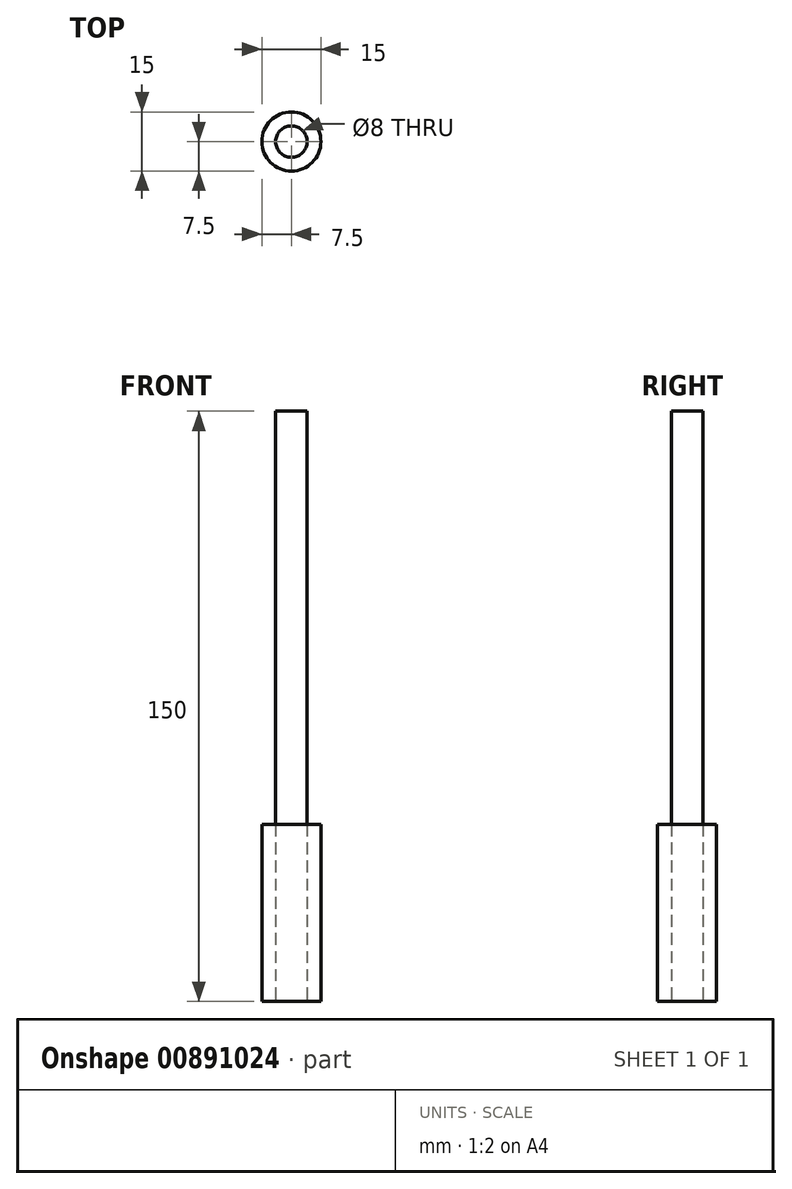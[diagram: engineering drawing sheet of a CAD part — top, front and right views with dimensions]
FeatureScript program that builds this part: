
annotation { "Feature Type Name" : "Feature", "Feature Type Description" : "" }
export const myFeature = defineFeature(function(context is Context, id is Id, definition is map)
    precondition{}
    {
        {
            var Q0;
            Q0=qCreatedBy(makeId("Top.planeOp"),FACE);
            var sketch = newSketch(context, id + "F0", { "sketchPlane" : qUnion([Q0])});
            skCircle(sketch, "E0", {"center": v(0, 0) * mm, "radius": 4 * mm});
            skSolve(sketch);
        }
        {
            var Q0;
            Q0=makeQuery(id+"F0.imprint","IMPRINT",FACE,{"disambiguationData":[TD([[makeQuery(id+"F0.imprint","IMPRINT",EDGE,{"derivedFrom":sQuery(id+"F0.wireOp",EDGE,"E0")}),1.0]])]});
            extrude(context, id + "F1", {"entities" : qUnion([Q0]), "depth" : 150 * mm, "offsetDistance" : 25 * mm});
        }
        {
            var Q0;
            Q0=qCreatedBy(makeId("Top.planeOp"),FACE);
            var sketch = newSketch(context, id + "F2", { "sketchPlane" : qUnion([Q0])});
            skCircle(sketch, "E1.0", {"center": v(0, 0) * mm, "radius": 4 * mm});
            skCircle(sketch, "E2", {"center": v(0, 0) * mm, "radius": 7.5 * mm});
            skSolve(sketch);
        }
        {
            var Q0;
            Q0=makeQuery(id+"F2.imprint","IMPRINT",FACE,{"disambiguationData":[TD([[makeQuery(id+"F2.imprint","IMPRINT",EDGE,{"derivedFrom":sQuery(id+"F2.wireOp",EDGE,"E1.0")}),-1.0]])]});
            extrude(context, id + "F3", {"entities" : qUnion([Q0]), "depth" : 45 * mm, "offsetDistance" : 25 * mm});
        }
    });
